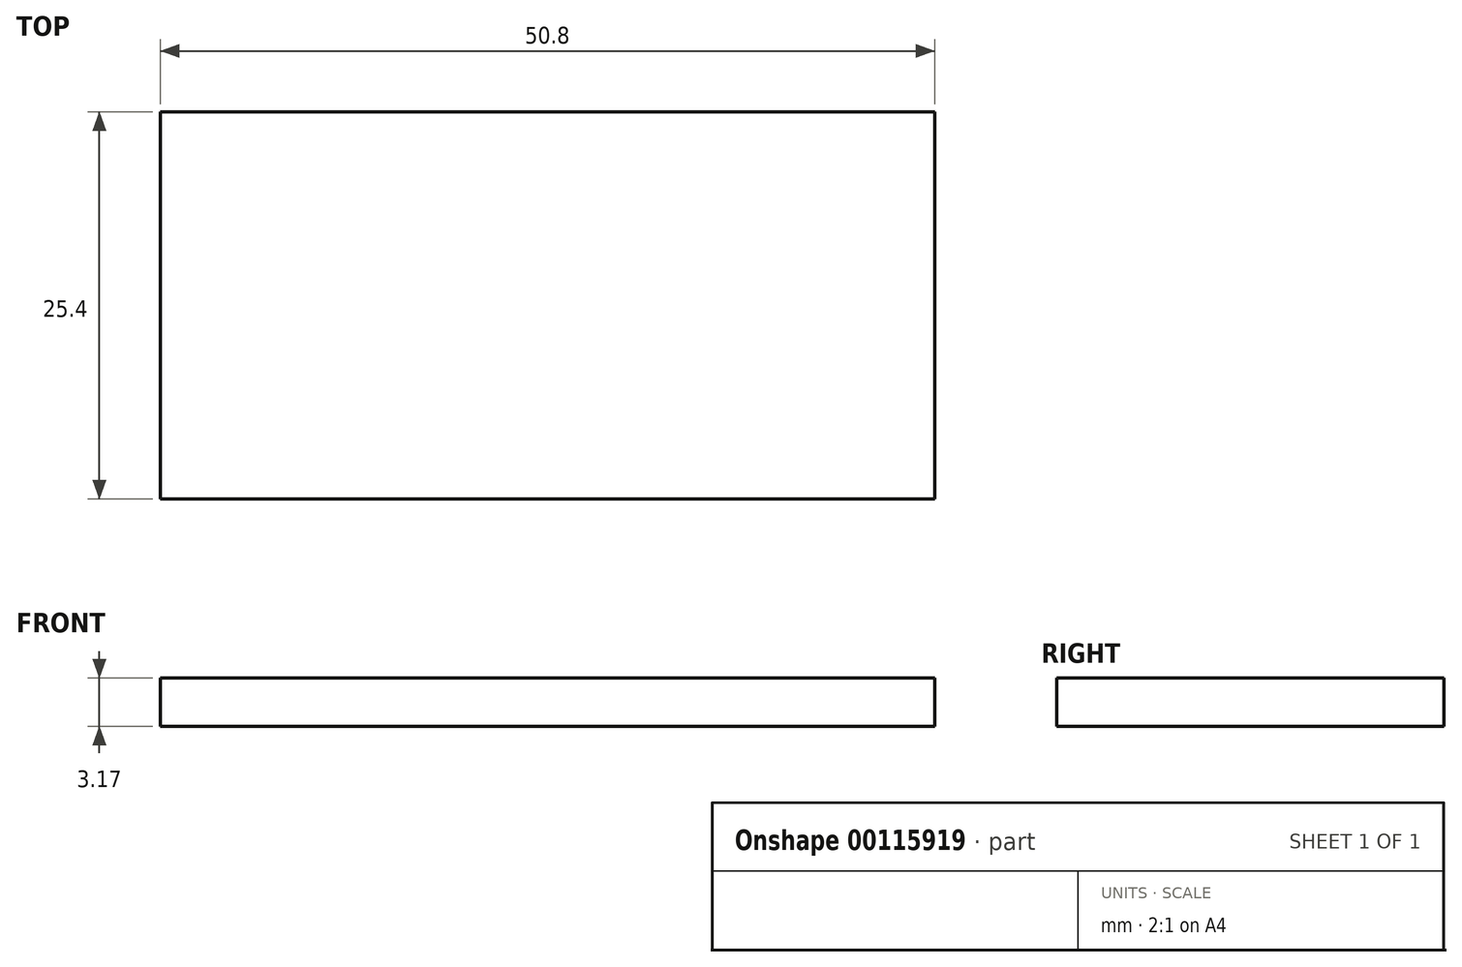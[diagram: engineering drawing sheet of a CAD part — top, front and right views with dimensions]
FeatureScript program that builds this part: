
annotation { "Feature Type Name" : "Feature", "Feature Type Description" : "" }
export const myFeature = defineFeature(function(context is Context, id is Id, definition is map)
    precondition{}
    {
        {
            var Q0;
            Q0=qCreatedBy(makeId("Top.planeOp"),FACE);
            var sketch = newSketch(context, id + "F0", { "sketchPlane" : qUnion([Q0])});
            skLineSegment(sketch, "E0.bottom", {"start": v(-26.34, 4.9) * mm, "end": v(24.46, 4.9) * mm});
            skLineSegment(sketch, "E0.top", {"start": v(-26.34, -20.5) * mm, "end": v(24.46, -20.5) * mm});
            skLineSegment(sketch, "E0.left", {"start": v(-26.34, 4.9) * mm, "end": v(-26.34, -20.5) * mm});
            skLineSegment(sketch, "E0.right", {"start": v(24.46, 4.9) * mm, "end": v(24.46, -20.5) * mm});
            skSolve(sketch);
        }
        {
            var Q0;
            Q0=makeQuery(id+"F0.imprint","IMPRINT",FACE,{"disambiguationData":[TD([[makeQuery(id+"F0.imprint","IMPRINT",EDGE,{"derivedFrom":sQuery(id+"F0.wireOp",EDGE,"E0.bottom")}),-1.0]])]});
            extrude(context, id + "F1", {"entities" : qUnion([Q0]), "depth" : 3.17 * mm});
        }
    });
